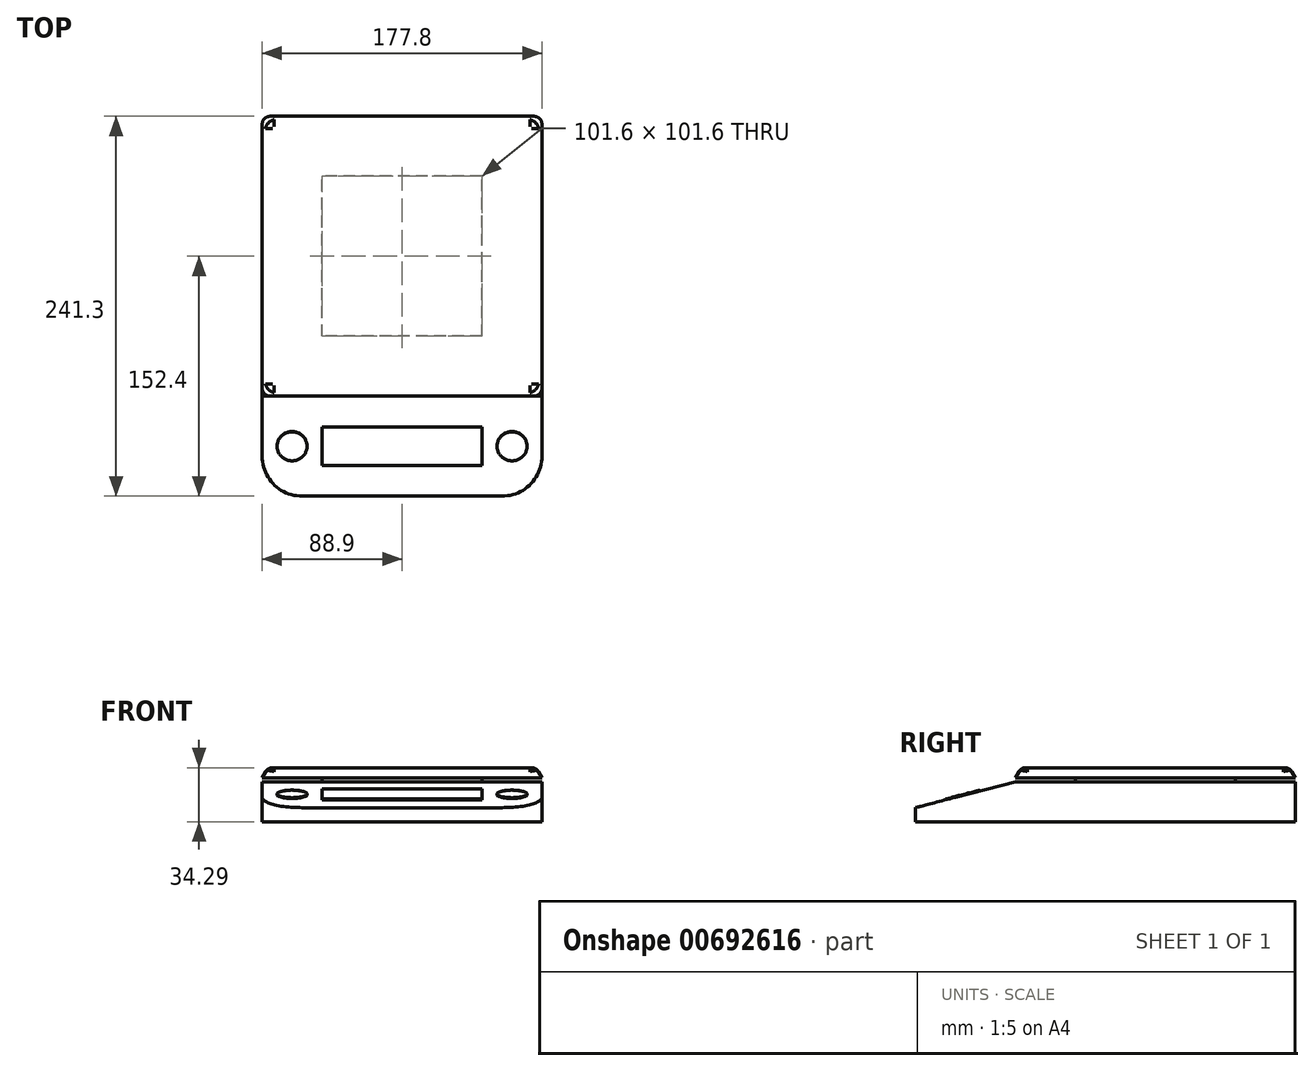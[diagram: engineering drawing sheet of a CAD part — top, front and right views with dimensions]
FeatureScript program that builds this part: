
annotation { "Feature Type Name" : "Feature", "Feature Type Description" : "" }
export const myFeature = defineFeature(function(context is Context, id is Id, definition is map)
    precondition{}
    {
        {
            var Q0;
            Q0=qCreatedBy(makeId("Top.planeOp"),FACE);
            var sketch = newSketch(context, id + "F0", { "sketchPlane" : qUnion([Q0])});
            skLineSegment(sketch, "E0.bottom", {"start": v(-88.9, 88.9) * mm, "end": v(88.9, 88.9) * mm});
            skLineSegment(sketch, "E0.top", {"start": v(-88.9, -152.4) * mm, "end": v(88.9, -152.4) * mm});
            skLineSegment(sketch, "E0.left", {"start": v(-88.9, 88.9) * mm, "end": v(-88.9, -152.4) * mm});
            skLineSegment(sketch, "E0.right", {"start": v(88.9, 88.9) * mm, "end": v(88.9, -88.9) * mm});
            skLineSegment(sketch, "E1", {"start": v(-88.9, -88.9) * mm, "end": v(88.9, -88.9) * mm});
            skLineSegment(sketch, "E2", {"start": v(88.9, -88.9) * mm, "end": v(-88.9, 88.9) * mm, "construction": true});
            skLineSegment(sketch, "E3", {"start": v(88.9, -88.9) * mm, "end": v(88.9, -152.4) * mm});
            skSolve(sketch);
        }
        {
            var Q0;
            Q0 = qSketchRegion(id + "F0", true);
            extrude(context, id + "F1", {"entities" : qUnion([Q0]), "depth" : 25.4 * mm, "offsetDistance" : 25.4 * mm});
        }
        {
            var Q0;
            Q0=qCreatedBy(makeId("Right.planeOp"),FACE);
            var sketch = newSketch(context, id + "F2", { "sketchPlane" : qUnion([Q0])});
            skLineSegment(sketch, "E4.bottom", {"start": v(-152.4, 8.9) * mm, "end": v(-88.9, 25.4) * mm});
            skLineSegment(sketch, "E4.top", {"start": v(-152.4, 25.4) * mm, "end": v(-88.9, 25.4) * mm});
            skLineSegment(sketch, "E4.left", {"start": v(-152.4, 8.9) * mm, "end": v(-152.4, 25.4) * mm});
            skSolve(sketch);
        }
        {
            var Q0;
            Q0 = qSketchRegion(id + "F2", true);
            extrude(context, id + "F3", {"entities" : qUnion([Q0]), "operationType" : NewBodyOperationType.REMOVE, "endBound" : BoundingType.THROUGH_ALL, "oppositeDirection" : true, "depth" : 25.4 * mm, "offsetDistance" : 25.4 * mm, "hasSecondDirection" : true, "secondDirectionBound" : SecondDirectionBoundingType.THROUGH_ALL, "secondDirectionOppositeDirection" : false, "secondDirectionDepth" : 25.4 * mm});
        }
        {
            var Q0;
            Q0=makeQuery(id+"F3.boolean.opBoolean","COPY",FACE,{"derivedFrom":makeQuery(id+"F3.opExtrude","SWEPT_FACE",FACE,{"disambiguationData":[OSD([sQuery(id+"F2.wireOp",EDGE,"E4.bottom")])]})});
            var sketch = newSketch(context, id + "F4", { "sketchPlane" : qUnion([Q0])});
            skLineSegment(sketch, "E5.bottom", {"start": v(50.8, -125.15) * mm, "end": v(-50.8, -125.15) * mm});
            skLineSegment(sketch, "E5.top", {"start": v(50.8, -99.75) * mm, "end": v(-50.8, -99.75) * mm});
            skLineSegment(sketch, "E5.left", {"start": v(50.8, -125.15) * mm, "end": v(50.8, -99.75) * mm});
            skLineSegment(sketch, "E5.right", {"start": v(-50.8, -125.15) * mm, "end": v(-50.8, -99.75) * mm});
            skPoint(sketch, "E5.middle", {"position": v(0, -112.45) * mm});
            skLineSegment(sketch, "E6", {"start": v(-88.9, -79.65) * mm, "end": v(88.9, -145.26) * mm, "construction": true});
            skCircle(sketch, "E7", {"center": v(-69.85, -112.45) * mm, "radius": 9.53 * mm});
            skLineSegment(sketch, "E8", {"start": v(-69.85, -112.45) * mm, "end": v(-50.8, -112.45) * mm, "construction": true});
            skLineSegment(sketch, "E9", {"start": v(-69.85, -112.45) * mm, "end": v(-88.9, -112.45) * mm, "construction": true});
            skLineSegment(sketch, "E10", {"start": v(0, -112.45) * mm, "end": v(0, -79.65) * mm, "construction": true});
            skCircle(sketch, "E11.MirrorC", {"center": v(69.85, -112.45) * mm, "radius": 9.53 * mm});
            skSolve(sketch);
        }
        {
            var Q0;
            Q0=makeQuery(id+"F1.opExtrude","SWEPT_EDGE",EDGE,{"disambiguationData":[OSD([sQuery(id+"F0.wireOp",EDGE,"E0.top"),sQuery(id+"F0.wireOp",EDGE,"E0.left")])]});
            var Q1;
            Q1=makeQuery(id+"F1.opExtrude","SWEPT_EDGE",EDGE,{"disambiguationData":[OSD([sQuery(id+"F0.wireOp",EDGE,"E0.top"),sQuery(id+"F0.wireOp",EDGE,"E3")])]});
            fillet(context, id + "F5", {"entities" : qUnion([Q0, Q1]), "radius" : 25.4 * mm, "tangentPropagation" : true, "allowEdgeOverflow" : false});
        }
        {
            var Q0;
            Q0 = qSketchRegion(id + "F4", true);
            extrude(context, id + "F6", {"entities" : qUnion([Q0]), "operationType" : NewBodyOperationType.ADD, "depth" : 0.5 * mm, "offsetDistance" : 25.4 * mm});
        }
        {
            var Q0;
            Q0=makeQuery(id+"F1.opExtrude","CAP_FACE",FACE,{"disambiguationData":[OSD([sQuery(id+"F0.wireOp",EDGE,"E0.bottom"),sQuery(id+"F0.wireOp",EDGE,"E0.top"),sQuery(id+"F0.wireOp",EDGE,"E0.left"),sQuery(id+"F0.wireOp",EDGE,"E0.right"),sQuery(id+"F0.wireOp",EDGE,"E3")])],"isStart":false});
            var sketch = newSketch(context, id + "F7", { "sketchPlane" : qUnion([Q0])});
            skLineSegment(sketch, "E12.bottom", {"start": v(50.8, -50.8) * mm, "end": v(-50.8, -50.8) * mm});
            skLineSegment(sketch, "E12.top", {"start": v(50.8, 50.8) * mm, "end": v(-50.8, 50.8) * mm});
            skLineSegment(sketch, "E12.left", {"start": v(50.8, -50.8) * mm, "end": v(50.8, 50.8) * mm});
            skLineSegment(sketch, "E12.right", {"start": v(-50.8, -50.8) * mm, "end": v(-50.8, 50.8) * mm});
            skPoint(sketch, "E12.middle", {"position": v(0, 0) * mm});
            skLineSegment(sketch, "E13", {"start": v(-50.8, 50.8) * mm, "end": v(50.8, -50.8) * mm, "construction": true});
            skSolve(sketch);
        }
        {
            var Q0;
            Q0 = qSketchRegion(id + "F7", true);
            extrude(context, id + "F8", {"entities" : qUnion([Q0]), "operationType" : NewBodyOperationType.ADD, "depth" : 2.54 * mm, "offsetDistance" : 25.4 * mm});
        }
        {
            var Q0;
            Q0=makeQuery(id+"F8.opExtrude","CAP_FACE",FACE,{"disambiguationData":[OSD([sQuery(id+"F7.wireOp",EDGE,"E12.bottom"),sQuery(id+"F7.wireOp",EDGE,"E12.top"),sQuery(id+"F7.wireOp",EDGE,"E12.left"),sQuery(id+"F7.wireOp",EDGE,"E12.right")])],"isStart":false});
            var sketch = newSketch(context, id + "F9", { "sketchPlane" : qUnion([Q0])});
            skLineSegment(sketch, "E14.bottom", {"start": v(88.9, -88.9) * mm, "end": v(-88.9, -88.9) * mm});
            skLineSegment(sketch, "E14.top", {"start": v(88.9, 88.9) * mm, "end": v(-88.9, 88.9) * mm});
            skLineSegment(sketch, "E14.left", {"start": v(88.9, -88.9) * mm, "end": v(88.9, 88.9) * mm});
            skLineSegment(sketch, "E14.right", {"start": v(-88.9, -88.9) * mm, "end": v(-88.9, 88.9) * mm});
            skPoint(sketch, "E14.middle", {"position": v(0, 0) * mm});
            skSolve(sketch);
        }
        {
            var Q0;
            Q0 = qSketchRegion(id + "F9", true);
            extrude(context, id + "F10", {"entities" : qUnion([Q0]), "operationType" : NewBodyOperationType.ADD, "depth" : 6.35 * mm, "offsetDistance" : 25.4 * mm, "hasDraft" : true, "draftAngle" : 30 * degree, "draftPullDirection" : true});
        }
        {
            var Q0;
            Q0=makeQuery(id+"F10.opExtrude","SWEPT_EDGE",EDGE,{"disambiguationData":[OSD([sQuery(id+"F9.wireOp",EDGE,"E14.bottom"),sQuery(id+"F9.wireOp",EDGE,"E14.left")])]});
            var Q1;
            Q1=makeQuery(id+"F10.opExtrude","SWEPT_EDGE",EDGE,{"disambiguationData":[OSD([sQuery(id+"F9.wireOp",EDGE,"E14.bottom"),sQuery(id+"F9.wireOp",EDGE,"E14.right")])]});
            var Q2;
            Q2=makeQuery(id+"F10.opExtrude","SWEPT_EDGE",EDGE,{"disambiguationData":[OSD([sQuery(id+"F9.wireOp",EDGE,"E14.top"),sQuery(id+"F9.wireOp",EDGE,"E14.left")])]});
            var Q3;
            Q3=makeQuery(id+"F1.opExtrude","SWEPT_EDGE",EDGE,{"disambiguationData":[OSD([sQuery(id+"F0.wireOp",EDGE,"E0.bottom"),sQuery(id+"F0.wireOp",EDGE,"E0.right")])]});
            var Q4;
            Q4=makeQuery(id+"F10.opExtrude","SWEPT_EDGE",EDGE,{"disambiguationData":[OSD([sQuery(id+"F9.wireOp",EDGE,"E14.top"),sQuery(id+"F9.wireOp",EDGE,"E14.right")])]});
            var Q5;
            Q5=makeQuery(id+"F1.opExtrude","SWEPT_EDGE",EDGE,{"disambiguationData":[OSD([sQuery(id+"F0.wireOp",EDGE,"E0.bottom"),sQuery(id+"F0.wireOp",EDGE,"E0.left")])]});
            fillet(context, id + "F11", {"entities" : qUnion([Q0, Q1, Q2, Q3, Q4, Q5]), "radius" : 6.35 * mm, "tangentPropagation" : true, "allowEdgeOverflow" : false});
        }
        {
            var Q0;
            Q0=makeQuery(id+"F10.opExtrude","CAP_EDGE",EDGE,{"disambiguationData":[OSD([sQuery(id+"F9.wireOp",EDGE,"E14.left")])],"isStart":false});
            var Q1;
            Q1=makeQuery(id+"F10.opExtrude","CAP_EDGE",EDGE,{"disambiguationData":[OSD([sQuery(id+"F9.wireOp",EDGE,"E14.bottom")])],"isStart":false});
            var Q2;
            Q2=makeQuery(id+"F10.opExtrude","CAP_EDGE",EDGE,{"disambiguationData":[OSD([sQuery(id+"F9.wireOp",EDGE,"E14.right")])],"isStart":false});
            var Q3;
            Q3=makeQuery(id+"F10.opExtrude","CAP_EDGE",EDGE,{"disambiguationData":[OSD([sQuery(id+"F9.wireOp",EDGE,"E14.top")])],"isStart":false});
            fillet(context, id + "F12", {"entities" : qUnion([Q0, Q1, Q2, Q3]), "radius" : 5.08 * mm, "tangentPropagation" : true, "allowEdgeOverflow" : false});
        }
    });
